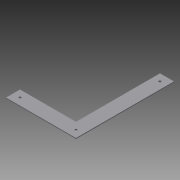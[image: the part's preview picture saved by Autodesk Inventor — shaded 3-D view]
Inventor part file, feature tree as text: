
AUTODESK INVENTOR PART (.ipt)
format: ipt  version: 2014 SP1 (Build 180222100, 222)  size: 86,016 bytes
history: native  units: in
note: dims shown in document units (in); Inventor stores cm internally (conversion verified against a paired STEP export)
features: sketch x2, extrude x1, hole x1
ambient origin geometry x8: Origin, YZ Plane, XZ Plane, XY Plane, X Axis, Y Axis, Z Axis, Center Point
bodies: Solid1 (feature_tree)
feature tree (4):
  extrude  "Extrusion1"  Depth=7.0in
  hole  "Hole1"  [1 undecoded]
  sketch  "Sketch1"  dims[d0=5.0in d1=7.0in]
  sketch  "Sketch2"  dims[d2=4.0in d3=6.0in d4=0.0625in d5=0.0in d6=0.5in d7=0.5in d8=0.165in d9=0.75in d10=0.375in d11=0.25in d12=0.5635in d13=1.0in d14=0.8108in]
note: 1 required parameter value undecoded (feature->parameter linkage not recoverable at this tier; creation-order binding heuristic only, values carry confidence <= 0.55)
